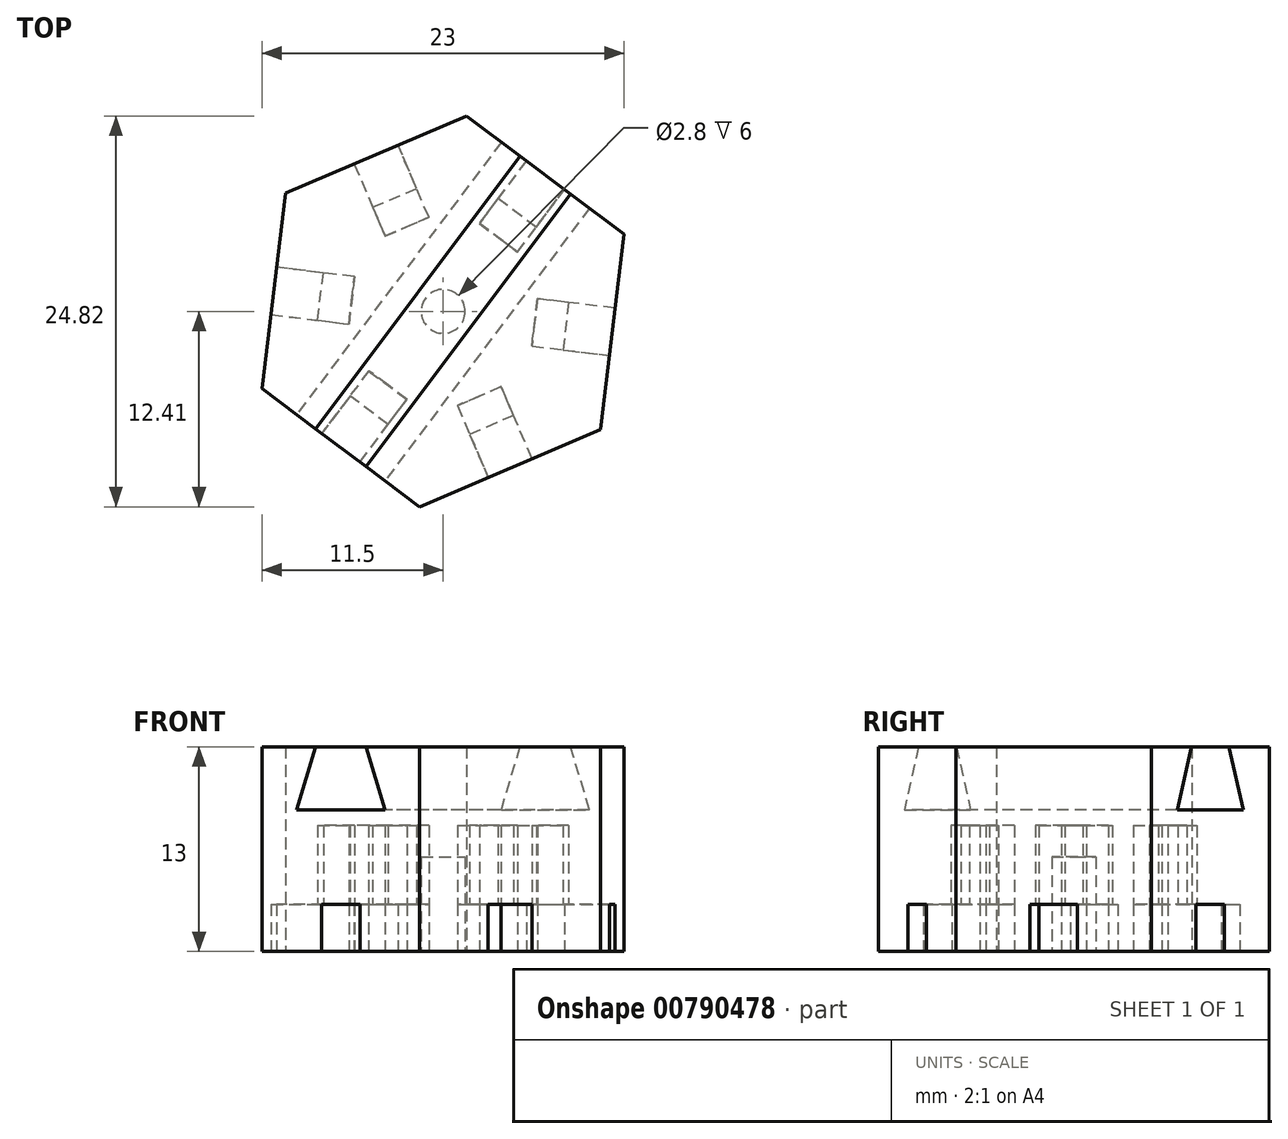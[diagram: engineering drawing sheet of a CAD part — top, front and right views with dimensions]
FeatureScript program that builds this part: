
annotation { "Feature Type Name" : "Feature", "Feature Type Description" : "" }
export const myFeature = defineFeature(function(context is Context, id is Id, definition is map)
    precondition{}
    {
        {
            var Q0;
            Q0=qCreatedBy(makeId("Top.planeOp"),FACE);
            var sketch = newSketch(context, id + "F0", { "sketchPlane" : qUnion([Q0])});
            skLineSegment(sketch, "E0.0", {"start": v(1.5, 12.41) * mm, "end": v(5.28, 9.57) * mm});
            skLineSegment(sketch, "E0.1", {"start": v(11.5, 4.91) * mm, "end": v(10.93, 0.2) * mm});
            skLineSegment(sketch, "E0.2", {"start": v(10, -7.5) * mm, "end": v(5.64, -9.36) * mm});
            skLineSegment(sketch, "E0.3", {"start": v(-1.5, -12.41) * mm, "end": v(-5.28, -9.57) * mm});
            skLineSegment(sketch, "E0.4", {"start": v(-11.5, -4.91) * mm, "end": v(-10.93, -0.2) * mm});
            skLineSegment(sketch, "E0.5", {"start": v(-10, 7.5) * mm, "end": v(-5.64, 9.36) * mm});
            skPoint(sketch, "E0.0.midPoint", {"position": v(6.5, 8.66) * mm});
            skPoint(sketch, "E1", {"position": v(-8.76, 1.06) * mm});
            skPoint(sketch, "E2", {"position": v(-3.47, 8.12) * mm});
            skPoint(sketch, "E3", {"position": v(5.3, 7.06) * mm});
            skPoint(sketch, "E4", {"position": v(3.47, -8.12) * mm});
            skPoint(sketch, "E5", {"position": v(-5.3, -7.06) * mm});
            skPoint(sketch, "E6", {"position": v(8.76, -1.06) * mm});
            skPoint(sketch, "E7.end.orphan", {"position": v(2.53, 8.63) * mm});
            skPoint(sketch, "E8.orphan", {"position": v(2.53, 11.63) * mm});
            skLineSegment(sketch, "E9", {"start": v(3.51, 4.68) * mm, "end": v(4.73, 3.78) * mm});
            skLineSegment(sketch, "E10", {"start": v(4.73, 3.78) * mm, "end": v(7.7, 7.75) * mm});
            skLineSegment(sketch, "E11", {"start": v(5.28, 9.57) * mm, "end": v(2.3, 5.59) * mm});
            skLineSegment(sketch, "E12", {"start": v(2.3, 5.59) * mm, "end": v(3.51, 4.68) * mm});
            skLineSegment(sketch, "E13.1.0", {"start": v(-5.64, 9.36) * mm, "end": v(-3.69, 4.78) * mm});
            skLineSegment(sketch, "E13.1.1", {"start": v(-2.3, 5.39) * mm, "end": v(-0.9, 5.98) * mm});
            skLineSegment(sketch, "E13.1.2", {"start": v(-0.9, 5.98) * mm, "end": v(-2.86, 10.55) * mm});
            skLineSegment(sketch, "E13.1.3", {"start": v(-3.69, 4.78) * mm, "end": v(-2.3, 5.39) * mm});
            skLineSegment(sketch, "E13.2.0", {"start": v(-10.93, -0.2) * mm, "end": v(-5.99, -0.8) * mm});
            skLineSegment(sketch, "E13.2.1", {"start": v(-5.81, 0.7) * mm, "end": v(-5.63, 2.2) * mm});
            skLineSegment(sketch, "E13.2.2", {"start": v(-5.63, 2.2) * mm, "end": v(-10.57, 2.8) * mm});
            skLineSegment(sketch, "E13.2.3", {"start": v(-5.99, -0.8) * mm, "end": v(-5.81, 0.7) * mm});
            skLineSegment(sketch, "E13.3.0", {"start": v(-5.28, -9.57) * mm, "end": v(-2.3, -5.59) * mm});
            skLineSegment(sketch, "E13.3.1", {"start": v(-3.51, -4.68) * mm, "end": v(-4.73, -3.78) * mm});
            skLineSegment(sketch, "E13.3.2", {"start": v(-4.73, -3.78) * mm, "end": v(-7.7, -7.75) * mm});
            skLineSegment(sketch, "E13.3.3", {"start": v(-2.3, -5.59) * mm, "end": v(-3.51, -4.68) * mm});
            skLineSegment(sketch, "E13.4.0", {"start": v(5.64, -9.36) * mm, "end": v(3.69, -4.78) * mm});
            skLineSegment(sketch, "E13.4.1", {"start": v(2.3, -5.39) * mm, "end": v(0.9, -5.98) * mm});
            skLineSegment(sketch, "E13.4.2", {"start": v(0.9, -5.98) * mm, "end": v(2.86, -10.55) * mm});
            skLineSegment(sketch, "E13.4.3", {"start": v(3.69, -4.78) * mm, "end": v(2.3, -5.39) * mm});
            skLineSegment(sketch, "E13.5.0", {"start": v(10.93, 0.2) * mm, "end": v(5.99, 0.8) * mm});
            skLineSegment(sketch, "E13.5.1", {"start": v(5.81, -0.7) * mm, "end": v(5.63, -2.2) * mm});
            skLineSegment(sketch, "E13.5.2", {"start": v(5.63, -2.2) * mm, "end": v(10.57, -2.8) * mm});
            skLineSegment(sketch, "E13.5.3", {"start": v(5.99, 0.8) * mm, "end": v(5.81, -0.7) * mm});
            skPoint(sketch, "E13.center", {"position": v(0, 0) * mm});
            skLineSegment(sketch, "E14.trimOffspring", {"start": v(7.7, 7.75) * mm, "end": v(11.5, 4.91) * mm});
            skArc(sketch, "E15.trimOffspring", {"start": v(10.82, 0.22) * mm, "mid": v(9.96, 4.25) * mm, "end": v(7.64, 7.67) * mm, "construction": true});
            skLineSegment(sketch, "E16.trimOffspring", {"start": v(10.57, -2.8) * mm, "end": v(10, -7.5) * mm});
            skLineSegment(sketch, "E17.trimOffspring", {"start": v(2.86, -10.55) * mm, "end": v(-1.5, -12.41) * mm});
            skLineSegment(sketch, "E18.trimOffspring", {"start": v(-7.7, -7.75) * mm, "end": v(-11.5, -4.91) * mm});
            skArc(sketch, "E19.trimOffspring", {"start": v(-10.82, -0.22) * mm, "mid": v(-9.96, -4.25) * mm, "end": v(-7.64, -7.67) * mm, "construction": true});
            skLineSegment(sketch, "E20.trimOffspring", {"start": v(-10.57, 2.8) * mm, "end": v(-10, 7.5) * mm});
            skArc(sketch, "E21.trimOffspring", {"start": v(-5.6, 9.26) * mm, "mid": v(-8.66, 6.5) * mm, "end": v(-10.46, 2.79) * mm, "construction": true});
            skLineSegment(sketch, "E22.trimOffspring", {"start": v(-2.86, 10.55) * mm, "end": v(1.5, 12.41) * mm});
            skPoint(sketch, "E23.0.start.orphan", {"position": v(-8.15, 6.11) * mm});
            skPoint(sketch, "E24.1.start.orphan", {"position": v(9.37, 4) * mm});
            skPoint(sketch, "E24.0.start.orphan", {"position": v(8.15, -6.11) * mm});
            skPoint(sketch, "E25.0.start.orphan", {"position": v(-1.22, -10.12) * mm});
            skPoint(sketch, "E26.0.start.orphan", {"position": v(-9.37, -4) * mm});
            skPoint(sketch, "E27.0.start.orphan", {"position": v(1.22, 10.12) * mm});
            skSolve(sketch);
        }
        {
            var Q0;
            Q0=qSketchRegion(id+"F0",true);
            extrude(context, id + "F1", {"entities" : qUnion([Q0]), "depth" : 3 * mm, "offsetDistance" : 25 * mm});
        }
        {
            var Q0;
            Q0=makeQuery(id+"F1.opExtrude","CAP_FACE",FACE,{"disambiguationData":[OSD([sQuery(id+"F0.wireOp",EDGE,"E0.0"),sQuery(id+"F0.wireOp",EDGE,"E0.1"),sQuery(id+"F0.wireOp",EDGE,"E0.2"),sQuery(id+"F0.wireOp",EDGE,"E0.3"),sQuery(id+"F0.wireOp",EDGE,"E0.4"),sQuery(id+"F0.wireOp",EDGE,"E0.5"),sQuery(id+"F0.wireOp",EDGE,"E9"),sQuery(id+"F0.wireOp",EDGE,"E10"),sQuery(id+"F0.wireOp",EDGE,"E11"),sQuery(id+"F0.wireOp",EDGE,"E12"),sQuery(id+"F0.wireOp",EDGE,"E13.1.0"),sQuery(id+"F0.wireOp",EDGE,"E13.1.1"),sQuery(id+"F0.wireOp",EDGE,"E13.1.2"),sQuery(id+"F0.wireOp",EDGE,"E13.1.3"),sQuery(id+"F0.wireOp",EDGE,"E13.2.0"),sQuery(id+"F0.wireOp",EDGE,"E13.2.1"),sQuery(id+"F0.wireOp",EDGE,"E13.2.2"),sQuery(id+"F0.wireOp",EDGE,"E13.2.3"),sQuery(id+"F0.wireOp",EDGE,"E13.3.0"),sQuery(id+"F0.wireOp",EDGE,"E13.3.1"),sQuery(id+"F0.wireOp",EDGE,"E13.3.2"),sQuery(id+"F0.wireOp",EDGE,"E13.3.3"),sQuery(id+"F0.wireOp",EDGE,"E13.4.0"),sQuery(id+"F0.wireOp",EDGE,"E13.4.1"),sQuery(id+"F0.wireOp",EDGE,"E13.4.2"),sQuery(id+"F0.wireOp",EDGE,"E13.4.3"),sQuery(id+"F0.wireOp",EDGE,"E13.5.0"),sQuery(id+"F0.wireOp",EDGE,"E13.5.1"),sQuery(id+"F0.wireOp",EDGE,"E13.5.2"),sQuery(id+"F0.wireOp",EDGE,"E13.5.3"),sQuery(id+"F0.wireOp",EDGE,"E14.trimOffspring"),sQuery(id+"F0.wireOp",EDGE,"E16.trimOffspring"),sQuery(id+"F0.wireOp",EDGE,"E17.trimOffspring"),sQuery(id+"F0.wireOp",EDGE,"E18.trimOffspring"),sQuery(id+"F0.wireOp",EDGE,"E20.trimOffspring"),sQuery(id+"F0.wireOp",EDGE,"E22.trimOffspring")])],"isStart":false});
            var sketch = newSketch(context, id + "F2", { "sketchPlane" : qUnion([Q0])});
            skCircle(sketch, "E28.cCircle", {"center": v(0, 0) * mm, "radius": 10.83 * mm, "construction": true});
            skLineSegment(sketch, "E28.0", {"start": v(-11.5, -4.91) * mm, "end": v(-10, 7.5) * mm});
            skLineSegment(sketch, "E28.1", {"start": v(-10, 7.5) * mm, "end": v(1.5, 12.41) * mm});
            skLineSegment(sketch, "E28.2", {"start": v(1.5, 12.41) * mm, "end": v(11.5, 4.91) * mm});
            skLineSegment(sketch, "E28.3", {"start": v(11.5, 4.91) * mm, "end": v(10, -7.5) * mm});
            skLineSegment(sketch, "E28.4", {"start": v(10, -7.5) * mm, "end": v(-1.5, -12.41) * mm});
            skLineSegment(sketch, "E28.5", {"start": v(-1.5, -12.41) * mm, "end": v(-11.5, -4.91) * mm});
            skPoint(sketch, "E28.0.midPoint", {"position": v(-10.75, 1.3) * mm});
            skLineSegment(sketch, "E29.0", {"start": v(-7.97, -0.56) * mm, "end": v(-7.6, 2.44) * mm});
            skLineSegment(sketch, "E30", {"start": v(-7.6, 2.44) * mm, "end": v(-5.63, 2.2) * mm});
            skLineSegment(sketch, "E31", {"start": v(-5.63, 2.2) * mm, "end": v(-5.99, -0.8) * mm});
            skLineSegment(sketch, "E32", {"start": v(-5.99, -0.8) * mm, "end": v(-7.97, -0.56) * mm});
            skLineSegment(sketch, "E33.1.0", {"start": v(-3.5, -7.19) * mm, "end": v(-5.92, -5.37) * mm});
            skLineSegment(sketch, "E33.1.1", {"start": v(-5.92, -5.37) * mm, "end": v(-4.73, -3.78) * mm});
            skLineSegment(sketch, "E33.1.2", {"start": v(-4.73, -3.78) * mm, "end": v(-2.3, -5.59) * mm});
            skLineSegment(sketch, "E33.1.3", {"start": v(-2.3, -5.59) * mm, "end": v(-3.5, -7.19) * mm});
            skLineSegment(sketch, "E33.2.0", {"start": v(4.47, -6.62) * mm, "end": v(1.69, -7.81) * mm});
            skLineSegment(sketch, "E33.2.1", {"start": v(1.69, -7.81) * mm, "end": v(0.9, -5.98) * mm});
            skLineSegment(sketch, "E33.2.2", {"start": v(0.9, -5.98) * mm, "end": v(3.69, -4.78) * mm});
            skLineSegment(sketch, "E33.2.3", {"start": v(3.69, -4.78) * mm, "end": v(4.47, -6.62) * mm});
            skLineSegment(sketch, "E33.3.0", {"start": v(7.97, 0.56) * mm, "end": v(7.6, -2.44) * mm});
            skLineSegment(sketch, "E33.3.1", {"start": v(7.6, -2.44) * mm, "end": v(5.63, -2.2) * mm});
            skLineSegment(sketch, "E33.3.2", {"start": v(5.63, -2.2) * mm, "end": v(5.99, 0.8) * mm});
            skLineSegment(sketch, "E33.3.3", {"start": v(5.99, 0.8) * mm, "end": v(7.97, 0.56) * mm});
            skLineSegment(sketch, "E33.4.0", {"start": v(3.5, 7.19) * mm, "end": v(5.92, 5.37) * mm});
            skLineSegment(sketch, "E33.4.1", {"start": v(5.92, 5.37) * mm, "end": v(4.73, 3.78) * mm});
            skLineSegment(sketch, "E33.4.2", {"start": v(4.73, 3.78) * mm, "end": v(2.3, 5.59) * mm});
            skLineSegment(sketch, "E33.4.3", {"start": v(2.3, 5.59) * mm, "end": v(3.5, 7.19) * mm});
            skLineSegment(sketch, "E33.5.0", {"start": v(-4.47, 6.62) * mm, "end": v(-1.69, 7.81) * mm});
            skLineSegment(sketch, "E33.5.1", {"start": v(-1.69, 7.81) * mm, "end": v(-0.9, 5.98) * mm});
            skLineSegment(sketch, "E33.5.2", {"start": v(-0.9, 5.98) * mm, "end": v(-3.69, 4.78) * mm});
            skLineSegment(sketch, "E33.5.3", {"start": v(-3.69, 4.78) * mm, "end": v(-4.47, 6.62) * mm});
            skSolve(sketch);
        }
        {
            var Q0;
            Q0=qSketchRegion(id+"F2",true);
            extrude(context, id + "F3", {"entities" : qUnion([Q0]), "operationType" : NewBodyOperationType.ADD, "depth" : 5 * mm, "offsetDistance" : 25 * mm});
        }
        {
            var Q0;
            Q0=makeQuery(id+"F3.opExtrude","CAP_FACE",FACE,{"disambiguationData":[OSD([sQuery(id+"F2.wireOp",EDGE,"E28.0"),sQuery(id+"F2.wireOp",EDGE,"E28.1"),sQuery(id+"F2.wireOp",EDGE,"E28.2"),sQuery(id+"F2.wireOp",EDGE,"E28.3"),sQuery(id+"F2.wireOp",EDGE,"E28.4"),sQuery(id+"F2.wireOp",EDGE,"E28.5"),sQuery(id+"F2.wireOp",EDGE,"E29.0"),sQuery(id+"F2.wireOp",EDGE,"E30"),sQuery(id+"F2.wireOp",EDGE,"E31"),sQuery(id+"F2.wireOp",EDGE,"E32"),sQuery(id+"F2.wireOp",EDGE,"E33.1.0"),sQuery(id+"F2.wireOp",EDGE,"E33.1.1"),sQuery(id+"F2.wireOp",EDGE,"E33.1.2"),sQuery(id+"F2.wireOp",EDGE,"E33.1.3"),sQuery(id+"F2.wireOp",EDGE,"E33.2.0"),sQuery(id+"F2.wireOp",EDGE,"E33.2.1"),sQuery(id+"F2.wireOp",EDGE,"E33.2.2"),sQuery(id+"F2.wireOp",EDGE,"E33.2.3"),sQuery(id+"F2.wireOp",EDGE,"E33.3.0"),sQuery(id+"F2.wireOp",EDGE,"E33.3.1"),sQuery(id+"F2.wireOp",EDGE,"E33.3.2"),sQuery(id+"F2.wireOp",EDGE,"E33.3.3"),sQuery(id+"F2.wireOp",EDGE,"E33.4.0"),sQuery(id+"F2.wireOp",EDGE,"E33.4.1"),sQuery(id+"F2.wireOp",EDGE,"E33.4.2"),sQuery(id+"F2.wireOp",EDGE,"E33.4.3"),sQuery(id+"F2.wireOp",EDGE,"E33.5.0"),sQuery(id+"F2.wireOp",EDGE,"E33.5.1"),sQuery(id+"F2.wireOp",EDGE,"E33.5.2"),sQuery(id+"F2.wireOp",EDGE,"E33.5.3")])],"isStart":false});
            var sketch = newSketch(context, id + "F4", { "sketchPlane" : qUnion([Q0])});
            skLineSegment(sketch, "E34.0", {"start": v(-1.5, -12.41) * mm, "end": v(-11.5, -4.91) * mm});
            skLineSegment(sketch, "E34.1", {"start": v(-10, 7.5) * mm, "end": v(1.5, 12.41) * mm});
            skLineSegment(sketch, "E34.2", {"start": v(1.5, 12.41) * mm, "end": v(11.5, 4.91) * mm});
            skLineSegment(sketch, "E34.3", {"start": v(-11.5, -4.91) * mm, "end": v(-10, 7.5) * mm});
            skLineSegment(sketch, "E34.4", {"start": v(11.5, 4.91) * mm, "end": v(10, -7.5) * mm});
            skLineSegment(sketch, "E34.5", {"start": v(10, -7.5) * mm, "end": v(-1.5, -12.41) * mm});
            skSolve(sketch);
        }
        {
            var Q0;
            Q0=qSketchRegion(id+"F4",true);
            extrude(context, id + "F5", {"entities" : qUnion([Q0]), "operationType" : NewBodyOperationType.ADD, "depth" : 5 * mm, "offsetDistance" : 25 * mm});
        }
        {
            var Q0;
            Q0=makeQuery(id+"F5.boolean.opBoolean","MERGE",FACE,{"derivedFrom":[makeQuery(id+"F3.boolean.opBoolean","MERGE",FACE,{"derivedFrom":[makeQuery(id+"F1.opExtrude","SWEPT_FACE",FACE,{"disambiguationData":[OSD([sQuery(id+"F0.wireOp",EDGE,"E0.3")])]}),makeQuery(id+"F1.opExtrude","SWEPT_FACE",FACE,{"disambiguationData":[OSD([sQuery(id+"F0.wireOp",EDGE,"E18.trimOffspring")])]}),makeQuery(id+"F3.opExtrude","SWEPT_FACE",FACE,{"disambiguationData":[OSD([sQuery(id+"F2.wireOp",EDGE,"E28.5")])]})]}),makeQuery(id+"F5.opExtrude","SWEPT_FACE",FACE,{"disambiguationData":[OSD([sQuery(id+"F4.wireOp",EDGE,"E34.0")])]})]});
            var sketch = newSketch(context, id + "F6", { "sketchPlane" : qUnion([Q0])});
            skLineSegment(sketch, "E35.bottom", {"start": v(3.5, 9) * mm, "end": v(-3.5, 9) * mm});
            skPoint(sketch, "E35.middle", {"position": v(0, 13) * mm});
            skLineSegment(sketch, "E36", {"start": v(-2, 13) * mm, "end": v(2, 13) * mm});
            skPoint(sketch, "E35.top.end.orphan", {"position": v(-3.5, 17) * mm});
            skPoint(sketch, "E37.orphan", {"position": v(3.5, 17) * mm});
            skPoint(sketch, "E38", {"position": v(-2, 13) * mm});
            skPoint(sketch, "E39", {"position": v(2, 13) * mm});
            skLineSegment(sketch, "E40", {"start": v(-2, 13) * mm, "end": v(-3.5, 9) * mm});
            skLineSegment(sketch, "E41", {"start": v(2, 13) * mm, "end": v(3.5, 9) * mm});
            skPoint(sketch, "E35.right.end.orphan", {"position": v(-3.5, 13) * mm});
            skPoint(sketch, "E35.left.end.orphan", {"position": v(3.5, 13) * mm});
            skSolve(sketch);
        }
        {
            var Q0;
            Q0=qSketchRegion(id+"F6",true);
            extrude(context, id + "F7", {"entities" : qUnion([Q0]), "operationType" : NewBodyOperationType.REMOVE, "endBound" : BoundingType.THROUGH_ALL, "oppositeDirection" : true, "depth" : 25 * mm, "offsetDistance" : 25 * mm});
        }
        {
            var Q0;
            Q0=makeQuery(id+"F1.opExtrude","CAP_FACE",FACE,{"disambiguationData":[OSD([sQuery(id+"F0.wireOp",EDGE,"E0.0"),sQuery(id+"F0.wireOp",EDGE,"E0.1"),sQuery(id+"F0.wireOp",EDGE,"E0.2"),sQuery(id+"F0.wireOp",EDGE,"E0.3"),sQuery(id+"F0.wireOp",EDGE,"E0.4"),sQuery(id+"F0.wireOp",EDGE,"E0.5"),sQuery(id+"F0.wireOp",EDGE,"E9"),sQuery(id+"F0.wireOp",EDGE,"E10"),sQuery(id+"F0.wireOp",EDGE,"E11"),sQuery(id+"F0.wireOp",EDGE,"E12"),sQuery(id+"F0.wireOp",EDGE,"E13.1.0"),sQuery(id+"F0.wireOp",EDGE,"E13.1.1"),sQuery(id+"F0.wireOp",EDGE,"E13.1.2"),sQuery(id+"F0.wireOp",EDGE,"E13.1.3"),sQuery(id+"F0.wireOp",EDGE,"E13.2.0"),sQuery(id+"F0.wireOp",EDGE,"E13.2.1"),sQuery(id+"F0.wireOp",EDGE,"E13.2.2"),sQuery(id+"F0.wireOp",EDGE,"E13.2.3"),sQuery(id+"F0.wireOp",EDGE,"E13.3.0"),sQuery(id+"F0.wireOp",EDGE,"E13.3.1"),sQuery(id+"F0.wireOp",EDGE,"E13.3.2"),sQuery(id+"F0.wireOp",EDGE,"E13.3.3"),sQuery(id+"F0.wireOp",EDGE,"E13.4.0"),sQuery(id+"F0.wireOp",EDGE,"E13.4.1"),sQuery(id+"F0.wireOp",EDGE,"E13.4.2"),sQuery(id+"F0.wireOp",EDGE,"E13.4.3"),sQuery(id+"F0.wireOp",EDGE,"E13.5.0"),sQuery(id+"F0.wireOp",EDGE,"E13.5.1"),sQuery(id+"F0.wireOp",EDGE,"E13.5.2"),sQuery(id+"F0.wireOp",EDGE,"E13.5.3"),sQuery(id+"F0.wireOp",EDGE,"E14.trimOffspring"),sQuery(id+"F0.wireOp",EDGE,"E16.trimOffspring"),sQuery(id+"F0.wireOp",EDGE,"E17.trimOffspring"),sQuery(id+"F0.wireOp",EDGE,"E18.trimOffspring"),sQuery(id+"F0.wireOp",EDGE,"E20.trimOffspring"),sQuery(id+"F0.wireOp",EDGE,"E22.trimOffspring")])],"isStart":true});
            var sketch = newSketch(context, id + "F8", { "sketchPlane" : qUnion([Q0])});
            skCircle(sketch, "E42", {"center": v(0, 0) * mm, "radius": 1.4 * mm});
            skSolve(sketch);
        }
        {
            var Q0;
            Q0=qSketchRegion(id+"F8",true);
            extrude(context, id + "F9", {"entities" : qUnion([Q0]), "operationType" : NewBodyOperationType.REMOVE, "oppositeDirection" : true, "depth" : 6 * mm, "offsetDistance" : 25 * mm});
        }
    });
